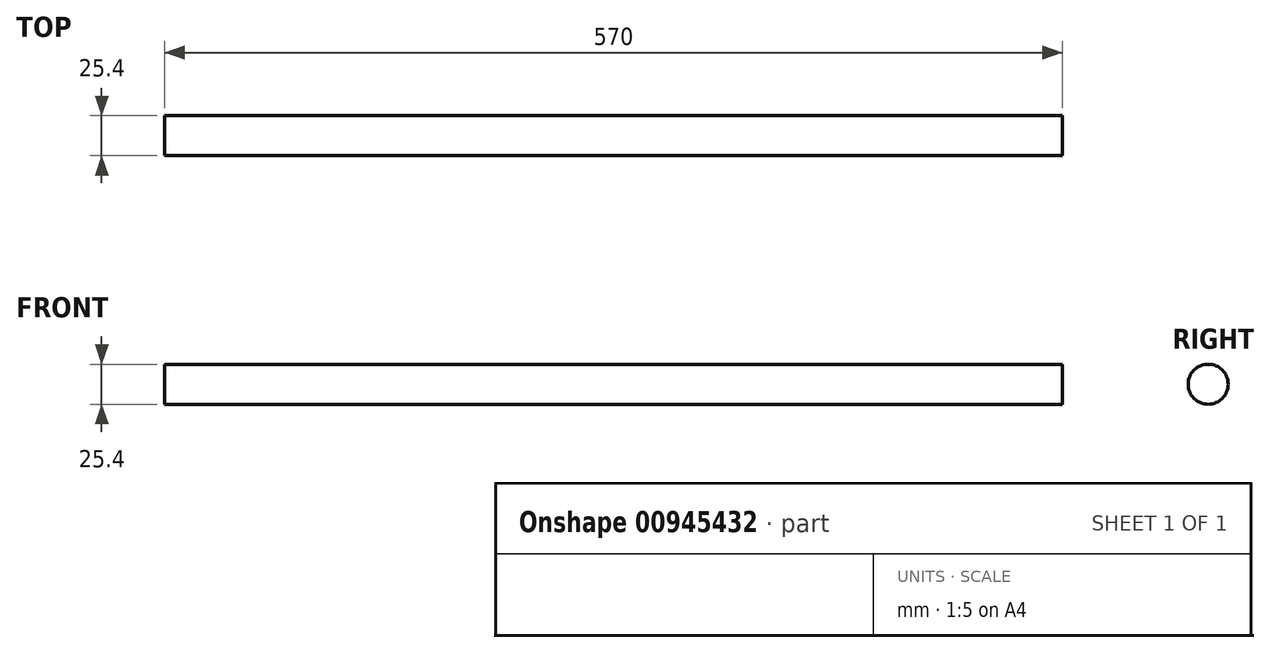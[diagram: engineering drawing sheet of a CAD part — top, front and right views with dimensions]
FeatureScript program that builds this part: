
annotation { "Feature Type Name" : "Feature", "Feature Type Description" : "" }
export const myFeature = defineFeature(function(context is Context, id is Id, definition is map)
    precondition{}
    {
        {
            var Q0;
            Q0=qCreatedBy(makeId("Right.planeOp"),FACE);
            var sketch = newSketch(context, id + "F0", { "sketchPlane" : qUnion([Q0])});
            skCircle(sketch, "E0", {"center": v(0, 0) * mm, "radius": 12.7 * mm});
            skSolve(sketch);
        }
        {
            var Q0;
            Q0=sQuery(id+"F0.wireOp",EDGE,"E0");
            extrude(context, id + "F1", {"bodyType" : ToolBodyType.SURFACE, "surfaceEntities" : qUnion([Q0]), "depth" : 570 * mm, "offsetDistance" : 25.4 * mm});
        }
    });
